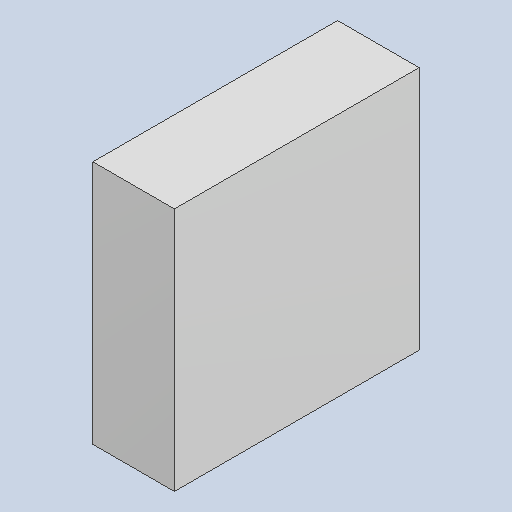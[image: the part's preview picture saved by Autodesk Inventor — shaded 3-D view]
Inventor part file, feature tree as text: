
AUTODESK INVENTOR PART (.ipt)
format: ipt  version: 2023.4 (Build 274418000, 418)  size: 81,408 bytes
history: native  units: mm
features: extrude x1
ambient origin geometry x8: Origin, YZ Plane, XZ Plane, XY Plane, X Axis, Y Axis, Z Axis, Center Point
bodies: Solid1 (feature_tree)
feature tree (1):
  extrude  "Extruded_37"  [1 undecoded]
note: 1 required parameter value undecoded (feature->parameter linkage not recoverable at this tier; creation-order binding heuristic only, values carry confidence <= 0.55)
